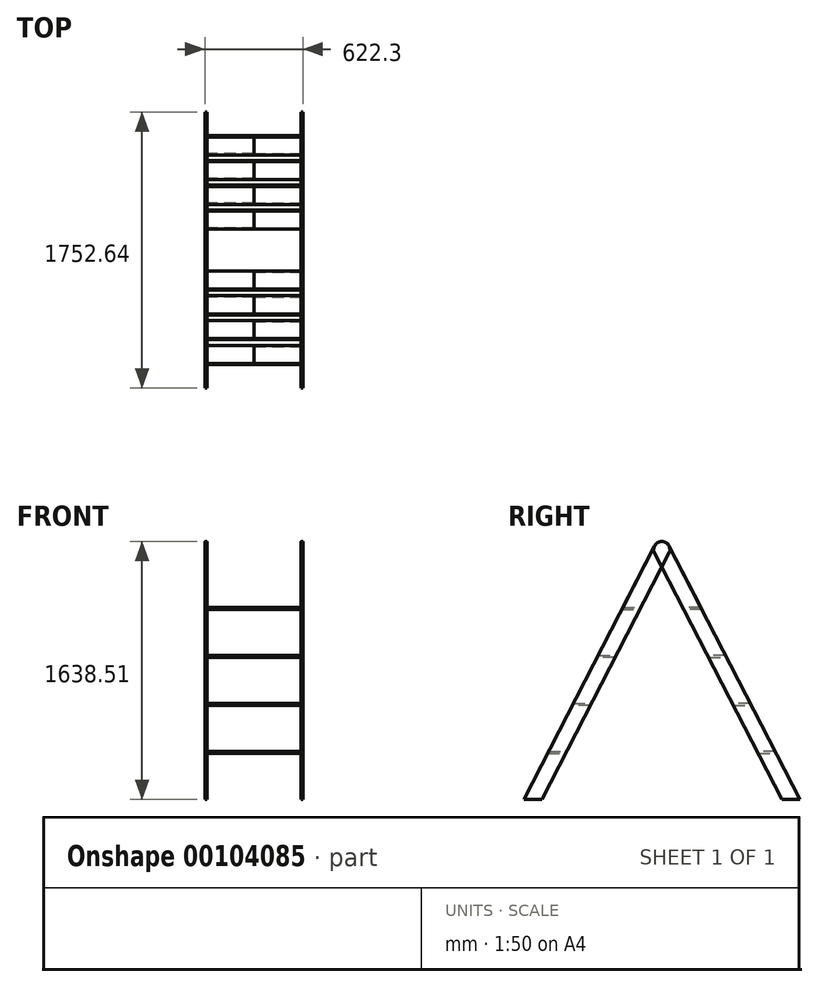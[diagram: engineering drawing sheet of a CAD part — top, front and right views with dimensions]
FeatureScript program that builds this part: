
annotation { "Feature Type Name" : "Feature", "Feature Type Description" : "" }
export const myFeature = defineFeature(function(context is Context, id is Id, definition is map)
    precondition{}
    {
        {
            var Q0;
            Q0=qCreatedBy(makeId("Right.planeOp"),FACE);
            var sketch = newSketch(context, id + "F0", { "sketchPlane" : qUnion([Q0])});
            skLineSegment(sketch, "E0", {"start": v(-876.32, 0) * mm, "end": v(-762, 0) * mm});
            skLineSegment(sketch, "E1", {"start": v(0, -99.18) * mm, "end": v(0, 1219.2) * mm, "construction": true});
            skLineSegment(sketch, "E2.0", {"start": v(-165.3, 1524) * mm, "end": v(213.23, 1524) * mm, "construction": true});
            skLineSegment(sketch, "E3.0", {"start": v(-762, -99.18) * mm, "end": v(-762, 109.7) * mm, "construction": true});
            skLineSegment(sketch, "E4", {"start": v(49.55, 1573.62) * mm, "end": v(-762, 0) * mm});
            skLineSegment(sketch, "E5.0", {"start": v(-719.12, 304.8) * mm, "end": v(160.9, 304.8) * mm, "construction": true});
            skLineSegment(sketch, "E6.0", {"start": v(-561.93, 609.6) * mm, "end": v(160.9, 609.6) * mm, "construction": true});
            skLineSegment(sketch, "E7.0", {"start": v(-404.74, 914.4) * mm, "end": v(160.9, 914.4) * mm, "construction": true});
            skLineSegment(sketch, "E8.0", {"start": v(-247.55, 1219.2) * mm, "end": v(160.9, 1219.2) * mm, "construction": true});
            skLineSegment(sketch, "E9.0", {"start": v(-45.65, 1610.7) * mm, "end": v(-876.32, 0) * mm});
            skPoint(sketch, "E10.orphan", {"position": v(-165.3, 0) * mm});
            skLineSegment(sketch, "E11.trimOffspring", {"start": v(0, 1524) * mm, "end": v(0, 1699.2) * mm, "construction": true});
            skArc(sketch, "E12", {"start": v(49.55, 1573.62) * mm, "mid": v(18.64, 1635) * mm, "end": v(-45.65, 1610.7) * mm});
            skPoint(sketch, "E13.orphan", {"position": v(23.96, 1524) * mm});
            skArc(sketch, "E14.trimOffspring", {"start": v(0, 1535.79) * mm, "mid": v(22, 1540.73) * mm, "end": v(39.75, 1554.63) * mm, "construction": true});
            skLineSegment(sketch, "E15.trimOffspring", {"start": v(-165.3, 0) * mm, "end": v(160.9, 0) * mm, "construction": true});
            skSolve(sketch);
        }
        {
            var Q0;
            Q0=makeQuery(id+"F0.imprint","IMPRINT",FACE,{"disambiguationData":[TD([[makeQuery(id+"F0.imprint","IMPRINT",EDGE,{"derivedFrom":sQuery(id+"F0.wireOp",EDGE,"E0")}),1.0]])]});
            var Q1;
            Q1=sQuery(id+"F0.wireOp",EDGE,"E4");
            extrude(context, id + "F1", {"entities" : qUnion([Q0]), "surfaceEntities" : qUnion([Q1]), "depth" : 12.7 * mm});
        }
        {
            var Q0;
            Q0=makeQuery(id+"F0.imprint","IMPRINT",FACE,{"disambiguationData":[TD([[makeQuery(id+"F0.imprint","IMPRINT",EDGE,{"derivedFrom":sQuery(id+"F0.wireOp",EDGE,"E0")}),1.0]])]});
            var sketch = newSketch(context, id + "F2", { "sketchPlane" : qUnion([Q0])});
            skLineSegment(sketch, "E16.0", {"start": v(-247.55, 1219.2) * mm, "end": v(-133.23, 1219.2) * mm});
            skLineSegment(sketch, "E17.0", {"start": v(-404.74, 914.4) * mm, "end": v(-290.42, 914.4) * mm});
            skLineSegment(sketch, "E18.0", {"start": v(-561.93, 609.6) * mm, "end": v(-447.62, 609.6) * mm});
            skLineSegment(sketch, "E19.0", {"start": v(-719.12, 304.8) * mm, "end": v(-604.8, 304.8) * mm});
            skLineSegment(sketch, "E20.0", {"start": v(-247.55, 1219.2) * mm, "end": v(-254.1, 1206.5) * mm});
            skLineSegment(sketch, "E21.0", {"start": v(-133.23, 1219.2) * mm, "end": v(-139.78, 1206.5) * mm});
            skLineSegment(sketch, "E22.0", {"start": v(-254.1, 1206.5) * mm, "end": v(-139.78, 1206.5) * mm});
            skLineSegment(sketch, "E23.0", {"start": v(-411.29, 901.7) * mm, "end": v(-296.97, 901.7) * mm});
            skLineSegment(sketch, "E24.0", {"start": v(-568.48, 596.9) * mm, "end": v(-454.17, 596.9) * mm});
            skLineSegment(sketch, "E25.0", {"start": v(-725.67, 292.1) * mm, "end": v(-611.36, 292.1) * mm});
            skPoint(sketch, "E26.orphan", {"position": v(49.55, 1573.62) * mm});
            skPoint(sketch, "E27.orphan", {"position": v(-45.65, 1610.7) * mm});
            skPoint(sketch, "E28.orphan", {"position": v(160.9, 1219.2) * mm});
            skLineSegment(sketch, "E29.trimOffspring", {"start": v(-290.42, 914.4) * mm, "end": v(-296.97, 901.7) * mm});
            skPoint(sketch, "E30.orphan", {"position": v(160.9, 914.4) * mm});
            skLineSegment(sketch, "E31.trimOffspring", {"start": v(-447.62, 609.6) * mm, "end": v(-454.17, 596.9) * mm});
            skLineSegment(sketch, "E32.trimOffspring", {"start": v(-561.93, 609.6) * mm, "end": v(-568.48, 596.9) * mm});
            skLineSegment(sketch, "E33.trimOffspring", {"start": v(-719.12, 304.8) * mm, "end": v(-725.67, 292.1) * mm});
            skLineSegment(sketch, "E34.trimOffspring", {"start": v(-604.8, 304.8) * mm, "end": v(-611.36, 292.1) * mm});
            skLineSegment(sketch, "E35.trimOffspring", {"start": v(-404.74, 914.4) * mm, "end": v(-411.29, 901.7) * mm});
            skPoint(sketch, "E36.orphan", {"position": v(160.9, 609.6) * mm});
            skPoint(sketch, "E37.orphan", {"position": v(160.9, 304.8) * mm});
            skPoint(sketch, "E38.orphan", {"position": v(-762, 0) * mm});
            skPoint(sketch, "E39.orphan", {"position": v(-876.32, 0) * mm});
            skSolve(sketch);
        }
        {
            var Q0;
            Q0 = qSketchRegion(id + "F2", true);
            extrude(context, id + "F3", {"entities" : qUnion([Q0]), "operationType" : NewBodyOperationType.REMOVE, "depth" : 6.35 * mm});
        }
        {
            var Q0;
            Q0=makeQuery(id+"F3.boolean.opBoolean","COPY",FACE,{"derivedFrom":makeQuery(id+"F3.opExtrude","CAP_FACE",FACE,{"disambiguationData":[OSD([sQuery(id+"F2.wireOp",EDGE,"E16.0"),sQuery(id+"F2.wireOp",EDGE,"E20.0"),sQuery(id+"F2.wireOp",EDGE,"E21.0"),sQuery(id+"F2.wireOp",EDGE,"E22.0")])],"isStart":false})});
            var sketch = newSketch(context, id + "F4", { "sketchPlane" : qUnion([Q0])});
            skLineSegment(sketch, "E40.0.0", {"start": v(247.55, 1219.2) * mm, "end": v(133.23, 1219.2) * mm});
            skLineSegment(sketch, "E40.0.1", {"start": v(133.23, 1219.2) * mm, "end": v(139.78, 1206.5) * mm});
            skLineSegment(sketch, "E40.0.2", {"start": v(139.78, 1206.5) * mm, "end": v(254.1, 1206.5) * mm});
            skLineSegment(sketch, "E40.0.3", {"start": v(254.1, 1206.5) * mm, "end": v(247.55, 1219.2) * mm});
            skLineSegment(sketch, "E41.0.0", {"start": v(404.74, 914.4) * mm, "end": v(290.42, 914.4) * mm});
            skLineSegment(sketch, "E41.0.1", {"start": v(290.42, 914.4) * mm, "end": v(296.97, 901.7) * mm});
            skLineSegment(sketch, "E41.0.2", {"start": v(296.97, 901.7) * mm, "end": v(411.29, 901.7) * mm});
            skLineSegment(sketch, "E41.0.3", {"start": v(411.29, 901.7) * mm, "end": v(404.74, 914.4) * mm});
            skLineSegment(sketch, "E42.0", {"start": v(45.65, 1610.7) * mm, "end": v(876.32, 0) * mm});
            skLineSegment(sketch, "E43.0.0", {"start": v(561.93, 609.6) * mm, "end": v(447.62, 609.6) * mm});
            skLineSegment(sketch, "E43.0.1", {"start": v(447.62, 609.6) * mm, "end": v(454.17, 596.9) * mm});
            skLineSegment(sketch, "E43.0.2", {"start": v(454.17, 596.9) * mm, "end": v(568.48, 596.9) * mm});
            skLineSegment(sketch, "E43.0.3", {"start": v(568.48, 596.9) * mm, "end": v(561.93, 609.6) * mm});
            skLineSegment(sketch, "E44.0.0", {"start": v(719.12, 304.8) * mm, "end": v(604.8, 304.8) * mm});
            skLineSegment(sketch, "E44.0.1", {"start": v(604.8, 304.8) * mm, "end": v(611.36, 292.1) * mm});
            skLineSegment(sketch, "E44.0.2", {"start": v(611.36, 292.1) * mm, "end": v(725.67, 292.1) * mm});
            skLineSegment(sketch, "E44.0.3", {"start": v(725.67, 292.1) * mm, "end": v(719.12, 304.8) * mm});
            skSolve(sketch);
        }
        {
            var Q0;
            Q0 = qSketchRegion(id + "F4", true);
            extrude(context, id + "F5", {"entities" : qUnion([Q0]), "depth" : 304.8 * mm});
        }
        {
            var Q0;
            Q0=makeQuery(id+"F1.opExtrude","SWEPT_BODY",BODY,{"disambiguationData":[OSD([sQuery(id+"F0.wireOp",EDGE,"E0"),sQuery(id+"F0.wireOp",EDGE,"E4"),sQuery(id+"F0.wireOp",EDGE,"E9.0"),sQuery(id+"F0.wireOp",EDGE,"E12")])]});
            var Q1;
            Q1=makeQuery(id+"F5.opExtrude","SWEPT_BODY",BODY,{"disambiguationData":[OSD([sQuery(id+"F4.wireOp",EDGE,"E40.0.0"),sQuery(id+"F4.wireOp",EDGE,"E40.0.1"),sQuery(id+"F4.wireOp",EDGE,"E40.0.2"),sQuery(id+"F4.wireOp",EDGE,"E42.0")])]});
            var Q2;
            Q2=makeQuery(id+"F5.opExtrude","SWEPT_BODY",BODY,{"disambiguationData":[OSD([sQuery(id+"F4.wireOp",EDGE,"E41.0.0"),sQuery(id+"F4.wireOp",EDGE,"E41.0.1"),sQuery(id+"F4.wireOp",EDGE,"E41.0.2"),sQuery(id+"F4.wireOp",EDGE,"E42.0")])]});
            var Q3;
            Q3=makeQuery(id+"F5.opExtrude","SWEPT_BODY",BODY,{"disambiguationData":[OSD([sQuery(id+"F4.wireOp",EDGE,"E43.0.0"),sQuery(id+"F4.wireOp",EDGE,"E43.0.1"),sQuery(id+"F4.wireOp",EDGE,"E43.0.2"),sQuery(id+"F4.wireOp",EDGE,"E43.0.3")])]});
            var Q4;
            Q4=makeQuery(id+"F5.opExtrude","SWEPT_BODY",BODY,{"disambiguationData":[OSD([sQuery(id+"F4.wireOp",EDGE,"E44.0.0"),sQuery(id+"F4.wireOp",EDGE,"E44.0.1"),sQuery(id+"F4.wireOp",EDGE,"E44.0.2"),sQuery(id+"F4.wireOp",EDGE,"E44.0.3")])]});
            var Q5;
            Q5=makeQuery(id+"F5.opExtrude","CAP_FACE",FACE,{"disambiguationData":[OSD([sQuery(id+"F4.wireOp",EDGE,"E40.0.0"),sQuery(id+"F4.wireOp",EDGE,"E40.0.1"),sQuery(id+"F4.wireOp",EDGE,"E40.0.2"),sQuery(id+"F4.wireOp",EDGE,"E42.0")])],"isStart":false});
            mirror(context, id + "F6", {"entities" : qUnion([Q0, Q1, Q2, Q3, Q4]), "mirrorPlane" : qUnion([Q5])});
        }
        {
            var Q0;
            Q0=makeQuery(id+"F1.opExtrude","SWEPT_BODY",BODY,{"disambiguationData":[OSD([sQuery(id+"F0.wireOp",EDGE,"E0"),sQuery(id+"F0.wireOp",EDGE,"E4"),sQuery(id+"F0.wireOp",EDGE,"E9.0"),sQuery(id+"F0.wireOp",EDGE,"E12")])]});
            var Q1;
            Q1=makeQuery(id+"F6.opPattern","COPY",BODY,{"derivedFrom":makeQuery(id+"F1.opExtrude","SWEPT_BODY",BODY,{"disambiguationData":[OSD([sQuery(id+"F0.wireOp",EDGE,"E0"),sQuery(id+"F0.wireOp",EDGE,"E4"),sQuery(id+"F0.wireOp",EDGE,"E9.0"),sQuery(id+"F0.wireOp",EDGE,"E12")])]}),"instanceName":"1"});
            var Q2;
            Q2=makeQuery(id+"F6.opPattern","COPY",BODY,{"derivedFrom":makeQuery(id+"F5.opExtrude","SWEPT_BODY",BODY,{"disambiguationData":[OSD([sQuery(id+"F4.wireOp",EDGE,"E40.0.0"),sQuery(id+"F4.wireOp",EDGE,"E40.0.1"),sQuery(id+"F4.wireOp",EDGE,"E40.0.2"),sQuery(id+"F4.wireOp",EDGE,"E42.0")])]}),"instanceName":"1"});
            var Q3;
            Q3=makeQuery(id+"F5.opExtrude","SWEPT_BODY",BODY,{"disambiguationData":[OSD([sQuery(id+"F4.wireOp",EDGE,"E40.0.0"),sQuery(id+"F4.wireOp",EDGE,"E40.0.1"),sQuery(id+"F4.wireOp",EDGE,"E40.0.2"),sQuery(id+"F4.wireOp",EDGE,"E42.0")])]});
            var Q4;
            Q4=makeQuery(id+"F5.opExtrude","SWEPT_BODY",BODY,{"disambiguationData":[OSD([sQuery(id+"F4.wireOp",EDGE,"E41.0.0"),sQuery(id+"F4.wireOp",EDGE,"E41.0.1"),sQuery(id+"F4.wireOp",EDGE,"E41.0.2"),sQuery(id+"F4.wireOp",EDGE,"E42.0")])]});
            var Q5;
            Q5=makeQuery(id+"F5.opExtrude","SWEPT_BODY",BODY,{"disambiguationData":[OSD([sQuery(id+"F4.wireOp",EDGE,"E43.0.0"),sQuery(id+"F4.wireOp",EDGE,"E43.0.1"),sQuery(id+"F4.wireOp",EDGE,"E43.0.2"),sQuery(id+"F4.wireOp",EDGE,"E43.0.3")])]});
            var Q6;
            Q6=makeQuery(id+"F5.opExtrude","SWEPT_BODY",BODY,{"disambiguationData":[OSD([sQuery(id+"F4.wireOp",EDGE,"E44.0.0"),sQuery(id+"F4.wireOp",EDGE,"E44.0.1"),sQuery(id+"F4.wireOp",EDGE,"E44.0.2"),sQuery(id+"F4.wireOp",EDGE,"E44.0.3")])]});
            var Q7;
            Q7=makeQuery(id+"F6.opPattern","COPY",BODY,{"derivedFrom":makeQuery(id+"F5.opExtrude","SWEPT_BODY",BODY,{"disambiguationData":[OSD([sQuery(id+"F4.wireOp",EDGE,"E41.0.0"),sQuery(id+"F4.wireOp",EDGE,"E41.0.1"),sQuery(id+"F4.wireOp",EDGE,"E41.0.2"),sQuery(id+"F4.wireOp",EDGE,"E42.0")])]}),"instanceName":"1"});
            var Q8;
            Q8=makeQuery(id+"F6.opPattern","COPY",BODY,{"derivedFrom":makeQuery(id+"F5.opExtrude","SWEPT_BODY",BODY,{"disambiguationData":[OSD([sQuery(id+"F4.wireOp",EDGE,"E43.0.0"),sQuery(id+"F4.wireOp",EDGE,"E43.0.1"),sQuery(id+"F4.wireOp",EDGE,"E43.0.2"),sQuery(id+"F4.wireOp",EDGE,"E43.0.3")])]}),"instanceName":"1"});
            var Q9;
            Q9=makeQuery(id+"F6.opPattern","COPY",BODY,{"derivedFrom":makeQuery(id+"F5.opExtrude","SWEPT_BODY",BODY,{"disambiguationData":[OSD([sQuery(id+"F4.wireOp",EDGE,"E44.0.0"),sQuery(id+"F4.wireOp",EDGE,"E44.0.1"),sQuery(id+"F4.wireOp",EDGE,"E44.0.2"),sQuery(id+"F4.wireOp",EDGE,"E44.0.3")])]}),"instanceName":"1"});
            var Q10;
            Q10=qCreatedBy(makeId("Front.planeOp"),FACE);
            mirror(context, id + "F7", {"entities" : qUnion([Q0, Q1, Q2, Q3, Q4, Q5, Q6, Q7, Q8, Q9]), "mirrorPlane" : qUnion([Q10])});
        }
    });
